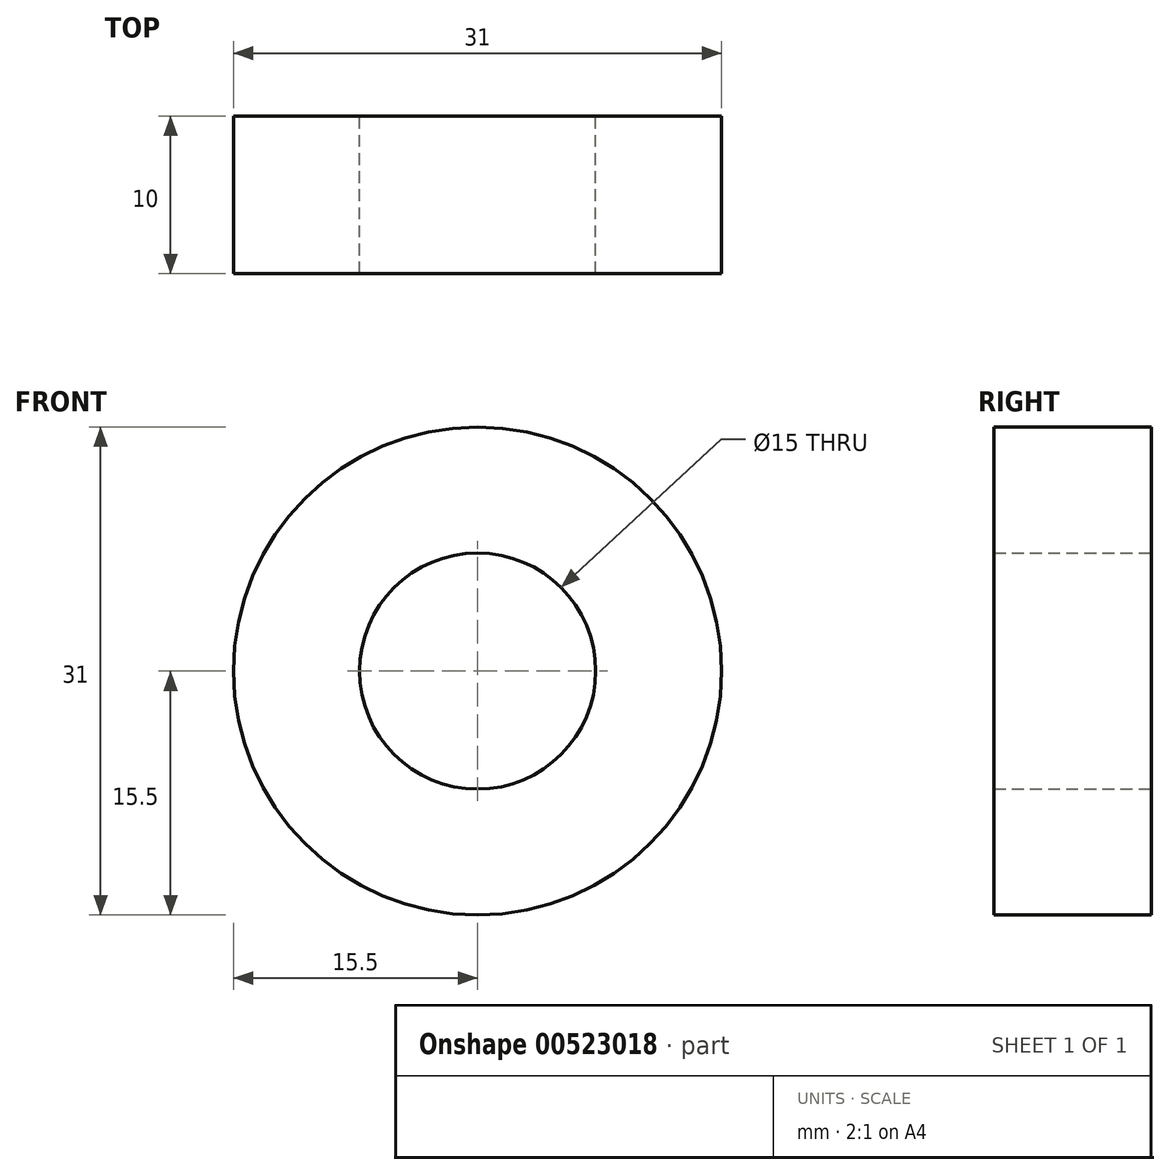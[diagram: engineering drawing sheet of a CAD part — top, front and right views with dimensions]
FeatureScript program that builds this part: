
annotation { "Feature Type Name" : "Feature", "Feature Type Description" : "" }
export const myFeature = defineFeature(function(context is Context, id is Id, definition is map)
    precondition{}
    {
        {
            var Q0;
            Q0=qCreatedBy(makeId("Front.planeOp"),FACE);
            var sketch = newSketch(context, id + "F0", { "sketchPlane" : qUnion([Q0])});
            skCircle(sketch, "E0", {"center": v(0, 0) * mm, "radius": 15.5 * mm});
            skCircle(sketch, "E1", {"center": v(0, 0) * mm, "radius": 7.5 * mm});
            skSolve(sketch);
        }
        {
            var Q0;
            Q0 = qSketchRegion(id + "F0", true);
            extrude(context, id + "F1", {"entities" : qUnion([Q0]), "endBound" : BoundingType.SYMMETRIC, "depth" : 10 * mm, "offsetDistance" : 25 * mm});
        }
    });
